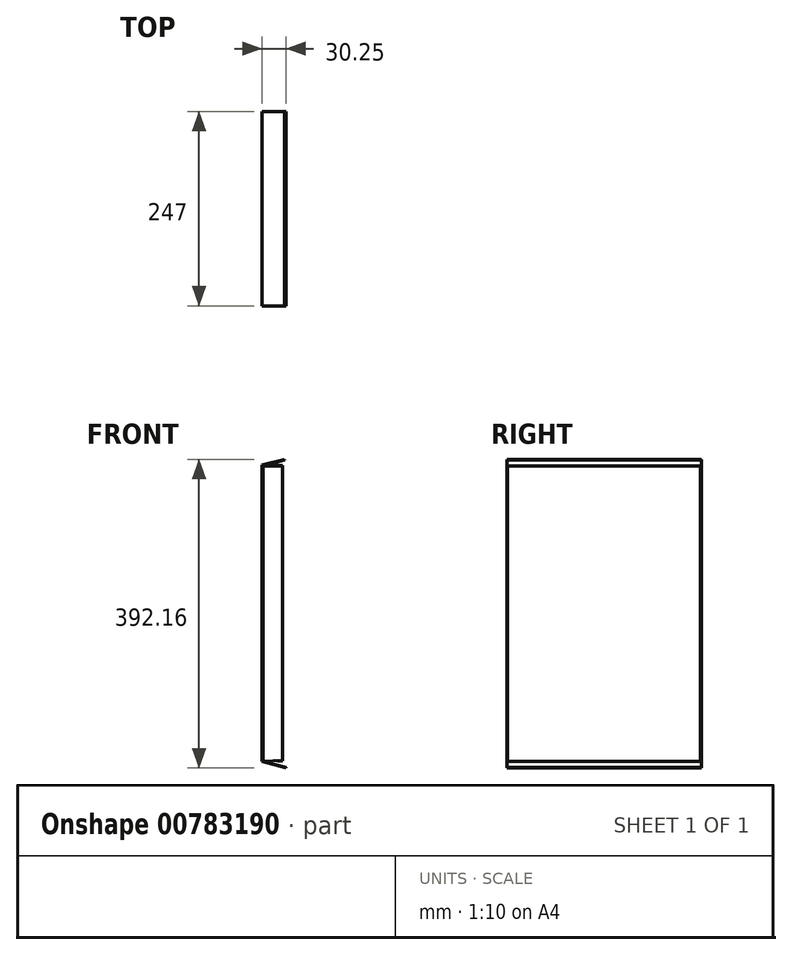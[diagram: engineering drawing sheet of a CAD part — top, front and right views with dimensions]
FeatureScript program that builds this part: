
annotation { "Feature Type Name" : "Feature", "Feature Type Description" : "" }
export const myFeature = defineFeature(function(context is Context, id is Id, definition is map)
    precondition{}
    {
        {
            var Q0;
            Q0=qCreatedBy(makeId("Front.planeOp"),FACE);
            var sketch = newSketch(context, id + "F0", { "sketchPlane" : qUnion([Q0])});
            skLineSegment(sketch, "E0", {"start": v(-1.12, 72.37) * mm, "end": v(-1.12, -302.63) * mm});
            skLineSegment(sketch, "E1", {"start": v(0, 71.86) * mm, "end": v(0, -303.14) * mm});
            skLineSegment(sketch, "E2.left", {"start": v(-1.12, 72.37) * mm, "end": v(-1.12, 73.37) * mm});
            skLineSegment(sketch, "E3.left", {"start": v(-1.12, -302.63) * mm, "end": v(-1.12, -303.63) * mm});
            skLineSegment(sketch, "E4", {"start": v(-1.12, 73.37) * mm, "end": v(27.33, 80.22) * mm});
            skLineSegment(sketch, "E5", {"start": v(27.33, 80.22) * mm, "end": v(27.56, 79.25) * mm});
            skLineSegment(sketch, "E6", {"start": v(27.56, 79.25) * mm, "end": v(0, 71.86) * mm});
            skLineSegment(sketch, "E7", {"start": v(0, -303.14) * mm, "end": v(29.13, -310.94) * mm});
            skLineSegment(sketch, "E8", {"start": v(29.13, -310.94) * mm, "end": v(29.13, -311.94) * mm});
            skLineSegment(sketch, "E9", {"start": v(29.13, -311.94) * mm, "end": v(-1.12, -303.63) * mm});
            skSolve(sketch);
        }
        {
            var Q0;
            {var subQ0=sQuery(id+"F0.wireOp",EDGE,"E0");Q0=makeQuery(id+"F0.imprint","IMPRINT",FACE,{"disambiguationData":[TD([[makeQuery(id+"F0.imprint","IMPRINT",EDGE,{"derivedFrom":subQ0}),1.0]])]});}
            var Q1;
            Q1=makeQuery(id+"F0.imprint","IMPRINT",FACE,{"disambiguationData":[TD([[makeQuery(id+"F0.imprint","IMPRINT",EDGE,{"derivedFrom":sQuery(id+"F0.wireOp",EDGE,"E3.top")}),1.0]])]});
            var Q2;
            Q2=makeQuery(id+"F0.imprint","IMPRINT",FACE,{"disambiguationData":[TD([[makeQuery(id+"F0.imprint","IMPRINT",EDGE,{"derivedFrom":sQuery(id+"F0.wireOp",EDGE,"E2.top")}),-1.0]])]});
            extrude(context, id + "F1", {"entities" : qUnion([Q0, Q1, Q2]), "depth" : 247 * mm, "offsetDistance" : 25 * mm});
        }
        {
            var Q0;
            Q0=qCreatedBy(makeId("Front.planeOp"),FACE);
            var sketch = newSketch(context, id + "F2", { "sketchPlane" : qUnion([Q0])});
            skLineSegment(sketch, "E10.bottom", {"start": v(24.9, 72.37) * mm, "end": v(-0.1, 72.37) * mm});
            skLineSegment(sketch, "E10.top", {"start": v(24.9, -302.63) * mm, "end": v(-0.1, -302.63) * mm});
            skLineSegment(sketch, "E10.left", {"start": v(24.9, 72.37) * mm, "end": v(24.9, -302.63) * mm});
            skLineSegment(sketch, "E10.right", {"start": v(-0.1, 72.37) * mm, "end": v(-0.1, -302.63) * mm});
            skLineSegment(sketch, "E11.bottom", {"start": v(186.82, 39.12) * mm, "end": v(643.37, 39.12) * mm});
            skLineSegment(sketch, "E11.top", {"start": v(186.82, -210.5) * mm, "end": v(643.37, -210.5) * mm});
            skLineSegment(sketch, "E11.left", {"start": v(186.82, 39.12) * mm, "end": v(186.82, -210.5) * mm});
            skLineSegment(sketch, "E11.right", {"start": v(643.37, 39.12) * mm, "end": v(643.37, -210.5) * mm});
            skLineSegment(sketch, "E12.bottom", {"start": v(-0.1, 71.37) * mm, "end": v(24.9, 71.37) * mm});
            skLineSegment(sketch, "E12.top", {"start": v(-0.1, -303.63) * mm, "end": v(24.9, -303.63) * mm});
            skLineSegment(sketch, "E12.left", {"start": v(-0.1, 71.37) * mm, "end": v(-0.1, -303.63) * mm});
            skLineSegment(sketch, "E12.right", {"start": v(24.9, 71.37) * mm, "end": v(24.9, -303.63) * mm});
            skSolve(sketch);
        }
        {
            var Q0;
            Q0=makeQuery(id+"F2.imprint","IMPRINT",FACE,{"disambiguationData":[TD([[makeQuery(id+"F2.imprint","IMPRINT",EDGE,{"derivedFrom":sQuery(id+"F2.wireOp",EDGE,"E10.bottom")}),1.0]])]});
            extrude(context, id + "F3", {"entities" : qUnion([Q0]), "operationType" : NewBodyOperationType.ADD, "depth" : 1 * mm, "offsetDistance" : 25 * mm});
        }
        {
            var Q0;
            {var subQ0=sQuery(id+"F2.wireOp",EDGE,"E10.top");Q0=makeQuery(id+"F2.imprint","IMPRINT",FACE,{"disambiguationData":[TD([[makeQuery(id+"F2.imprint","IMPRINT",EDGE,{"derivedFrom":subQ0}),-1.0]])]});}
            extrude(context, id + "F4", {"entities" : qUnion([Q0]), "operationType" : NewBodyOperationType.ADD, "depth" : 1 * mm, "offsetDistance" : 25 * mm});
        }
        {
            var Q0;
            Q0=makeQuery(id+"F1.opExtrude","CAP_FACE",FACE,{"disambiguationData":[OSD([sQuery(id+"F0.wireOp",EDGE,"E0"),sQuery(id+"F0.wireOp",EDGE,"E1"),sQuery(id+"F0.wireOp",EDGE,"E2.left"),sQuery(id+"F0.wireOp",EDGE,"E3.left"),sQuery(id+"F0.wireOp",EDGE,"E4"),sQuery(id+"F0.wireOp",EDGE,"E5"),sQuery(id+"F0.wireOp",EDGE,"E6"),sQuery(id+"F0.wireOp",EDGE,"E7"),sQuery(id+"F0.wireOp",EDGE,"E8"),sQuery(id+"F0.wireOp",EDGE,"E9")])],"isStart":false});
            var sketch = newSketch(context, id + "F5", { "sketchPlane" : qUnion([Q0])});
            skLineSegment(sketch, "E13", {"start": v(0, 71.86) * mm, "end": v(24.57, 71.86) * mm});
            skLineSegment(sketch, "E14", {"start": v(24.57, 71.86) * mm, "end": v(24.57, -302.46) * mm});
            skLineSegment(sketch, "E15", {"start": v(24.57, -302.46) * mm, "end": v(0, -303.14) * mm});
            skLineSegment(sketch, "E16", {"start": v(0, -303.14) * mm, "end": v(0, 71.86) * mm});
            skLineSegment(sketch, "E17", {"start": v(24.57, 71.86) * mm, "end": v(0, 71.86) * mm});
            skSolve(sketch);
        }
        {
            var Q0;
            Q0=makeQuery(id+"F5.imprint","IMPRINT",FACE,{"disambiguationData":[TD([[makeQuery(id+"F5.imprint","IMPRINT",EDGE,{"derivedFrom":sQuery(id+"F5.wireOp",EDGE,"E14")}),-1.0]])]});
            extrude(context, id + "F6", {"entities" : qUnion([Q0]), "oppositeDirection" : true, "depth" : 1 * mm, "offsetDistance" : 25 * mm});
        }
    });
